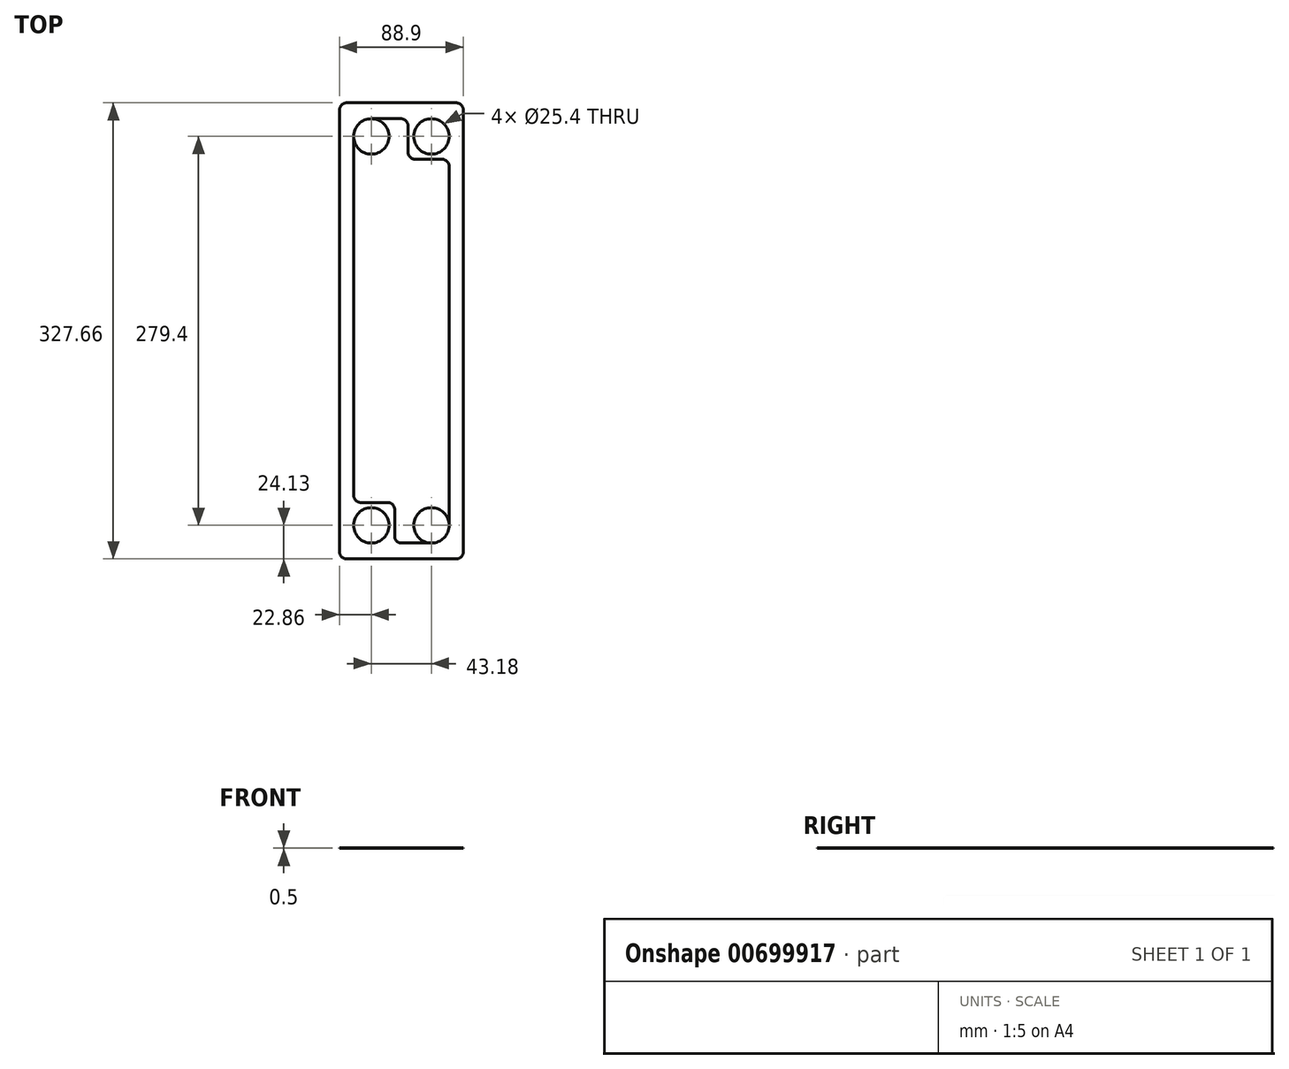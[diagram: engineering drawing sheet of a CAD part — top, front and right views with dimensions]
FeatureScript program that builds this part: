
annotation { "Feature Type Name" : "Feature", "Feature Type Description" : "" }
export const myFeature = defineFeature(function(context is Context, id is Id, definition is map)
    precondition{}
    {
        {
            var Q0;
            Q0=qCreatedBy(makeId("Top.planeOp"),FACE);
            var sketch = newSketch(context, id + "F0", { "sketchPlane" : qUnion([Q0])});
            skLineSegment(sketch, "E0.bottom", {"start": v(44.45, 163.83) * mm, "end": v(-44.45, 163.83) * mm});
            skLineSegment(sketch, "E0.top", {"start": v(44.45, -163.83) * mm, "end": v(-44.45, -163.83) * mm});
            skLineSegment(sketch, "E0.left", {"start": v(44.45, 163.83) * mm, "end": v(44.45, -163.83) * mm});
            skLineSegment(sketch, "E0.right", {"start": v(-44.45, 163.83) * mm, "end": v(-44.45, -163.83) * mm});
            skPoint(sketch, "E1", {"position": v(-21.6, 139.7) * mm});
            skPoint(sketch, "E2", {"position": v(21.59, -139.7) * mm});
            skCircle(sketch, "E3", {"center": v(-21.6, 139.7) * mm, "radius": 12.7 * mm});
            skCircle(sketch, "E4.MirrorC", {"center": v(21.6, -139.7) * mm, "radius": 12.7 * mm});
            skCircle(sketch, "E5.MirrorC", {"center": v(21.6, 139.7) * mm, "radius": 12.7 * mm});
            skCircle(sketch, "E6.MirrorC", {"center": v(-21.6, -139.7) * mm, "radius": 12.7 * mm});
            skLineSegment(sketch, "E7", {"start": v(34.3, -139.7) * mm, "end": v(34.3, 123.3) * mm});
            skLineSegment(sketch, "E8", {"start": v(-21.6, 152.4) * mm, "end": v(4.83, 152.4) * mm});
            skLineSegment(sketch, "E9", {"start": v(34.3, 123.3) * mm, "end": v(4.83, 123.3) * mm});
            skLineSegment(sketch, "E10", {"start": v(4.83, 123.3) * mm, "end": v(4.83, 152.4) * mm});
            skLineSegment(sketch, "E11", {"start": v(21.59, -152.4) * mm, "end": v(-4.83, -152.4) * mm});
            skLineSegment(sketch, "E12", {"start": v(-4.83, -152.4) * mm, "end": v(-4.83, -123.3) * mm});
            skLineSegment(sketch, "E13", {"start": v(-34.3, 139.7) * mm, "end": v(-34.3, -123.3) * mm});
            skLineSegment(sketch, "E14", {"start": v(-34.3, -123.3) * mm, "end": v(-4.83, -123.3) * mm});
            skSolve(sketch);
        }
        {
            var Q0;
            Q0=makeQuery(id+"F0.imprint","IMPRINT",FACE,{"disambiguationData":[TD([[makeQuery(id+"F0.imprint","IMPRINT",EDGE,{"derivedFrom":sQuery(id+"F0.wireOp",EDGE,"E0.bottom")}),1.0]])]});
            extrude(context, id + "F1", {"entities" : qUnion([Q0]), "depth" : 0.5 * mm, "offsetDistance" : 25.4 * mm});
        }
        {
            var Q0;
            {var subQ1=sQuery(id+"F0.wireOp",EDGE,"uRbJ42Cn-RmUv-xTCl-n5TW-Qzyheg3At7g8");Q0=makeQuery(id+"F0.imprint","IMPRINT",FACE,{"disambiguationData":[TD([[makeQuery(id+"F0.imprint","IMPRINT",EDGE,{"derivedFrom":subQ1}),-1.0]])]});}
            var Q1;
            {var subQ1=sQuery(id+"F0.wireOp",EDGE,"HQSko3t3-Edfd-RaWb-oDFQ-6hVYlKDIakkC");Q1=makeQuery(id+"F0.imprint","IMPRINT",FACE,{"disambiguationData":[TD([[makeQuery(id+"F0.imprint","IMPRINT",EDGE,{"derivedFrom":subQ1}),-1.0]])]});}
            var Q2;
            {var subQ1=sQuery(id+"F0.wireOp",EDGE,"E7");Q2=makeQuery(id+"F0.imprint","IMPRINT",FACE,{"disambiguationData":[TD([[makeQuery(id+"F0.imprint","IMPRINT",EDGE,{"derivedFrom":subQ1}),1.0]])]});}
            extrude(context, id + "F2", {"entities" : qUnion([Q0, Q1, Q2]), "operationType" : NewBodyOperationType.ADD, "depth" : 0 * mm, "offsetDistance" : 25.4 * mm});
        }
        {
            var Q0;
            Q0=makeQuery(id+"F1.opExtrude","SWEPT_EDGE",EDGE,{"disambiguationData":[OSD([sQuery(id+"F0.wireOp",EDGE,"HQSko3t3-Edfd-RaWb-oDFQ-6hVYlKDIakkC"),sQuery(id+"F0.wireOp",EDGE,"il05OQOl-aZX7-83aE-6OV3-z7G8VeRaLPhr")])]});
            var Q1;
            Q1=makeQuery(id+"F1.opExtrude","SWEPT_EDGE",EDGE,{"disambiguationData":[OSD([sQuery(id+"F0.wireOp",EDGE,"mnE11Z5x-ecDT-Nnf1-er53-Xfubo6Nqn0BC"),sQuery(id+"F0.wireOp",EDGE,"il05OQOl-aZX7-83aE-6OV3-z7G8VeRaLPhr")])]});
            var Q2;
            Q2=makeQuery(id+"F1.opExtrude","SWEPT_EDGE",EDGE,{"disambiguationData":[OSD([sQuery(id+"F0.wireOp",EDGE,"E0.bottom"),sQuery(id+"F0.wireOp",EDGE,"E0.right")])]});
            var Q3;
            Q3=makeQuery(id+"F1.opExtrude","SWEPT_EDGE",EDGE,{"disambiguationData":[OSD([sQuery(id+"F0.wireOp",EDGE,"E0.top"),sQuery(id+"F0.wireOp",EDGE,"E0.left")])]});
            var Q4;
            Q4=makeQuery(id+"F1.opExtrude","SWEPT_EDGE",EDGE,{"disambiguationData":[OSD([sQuery(id+"F0.wireOp",EDGE,"E0.top"),sQuery(id+"F0.wireOp",EDGE,"E0.right")])]});
            var Q5;
            Q5=makeQuery(id+"F1.opExtrude","SWEPT_EDGE",EDGE,{"disambiguationData":[OSD([sQuery(id+"F0.wireOp",EDGE,"E0.bottom"),sQuery(id+"F0.wireOp",EDGE,"E0.left")])]});
            var Q6;
            Q6=makeQuery(id+"F1.opExtrude","SWEPT_EDGE",EDGE,{"disambiguationData":[OSD([sQuery(id+"F0.wireOp",EDGE,"uRbJ42Cn-RmUv-xTCl-n5TW-Qzyheg3At7g8"),sQuery(id+"F0.wireOp",EDGE,"wbDQwIlr-Qm1d-dVtH-RILK-g2yp7KXGbha7")])]});
            var Q7;
            Q7=makeQuery(id+"F1.opExtrude","SWEPT_EDGE",EDGE,{"disambiguationData":[OSD([sQuery(id+"F0.wireOp",EDGE,"E8"),sQuery(id+"F0.wireOp",EDGE,"E10")])]});
            var Q8;
            Q8=makeQuery(id+"F1.opExtrude","SWEPT_EDGE",EDGE,{"disambiguationData":[OSD([sQuery(id+"F0.wireOp",EDGE,"E9"),sQuery(id+"F0.wireOp",EDGE,"E10")])]});
            var Q9;
            Q9=makeQuery(id+"F1.opExtrude","SWEPT_EDGE",EDGE,{"disambiguationData":[OSD([sQuery(id+"F0.wireOp",EDGE,"E7"),sQuery(id+"F0.wireOp",EDGE,"E9")])]});
            var Q10;
            Q10=makeQuery(id+"F1.opExtrude","SWEPT_EDGE",EDGE,{"disambiguationData":[OSD([sQuery(id+"F0.wireOp",EDGE,"E11"),sQuery(id+"F0.wireOp",EDGE,"E12")])]});
            var Q11;
            Q11=makeQuery(id+"F1.opExtrude","SWEPT_EDGE",EDGE,{"disambiguationData":[OSD([sQuery(id+"F0.wireOp",EDGE,"E12"),sQuery(id+"F0.wireOp",EDGE,"E14")])]});
            var Q12;
            Q12=makeQuery(id+"F1.opExtrude","SWEPT_EDGE",EDGE,{"disambiguationData":[OSD([sQuery(id+"F0.wireOp",EDGE,"E13"),sQuery(id+"F0.wireOp",EDGE,"E14")])]});
            fillet(context, id + "F3", {"entities" : qUnion([Q0, Q1, Q2, Q3, Q4, Q5, Q6, Q7, Q8, Q9, Q10, Q11, Q12]), "radius" : 5.08 * mm, "tangentPropagation" : true, "allowEdgeOverflow" : false});
        }
    });
